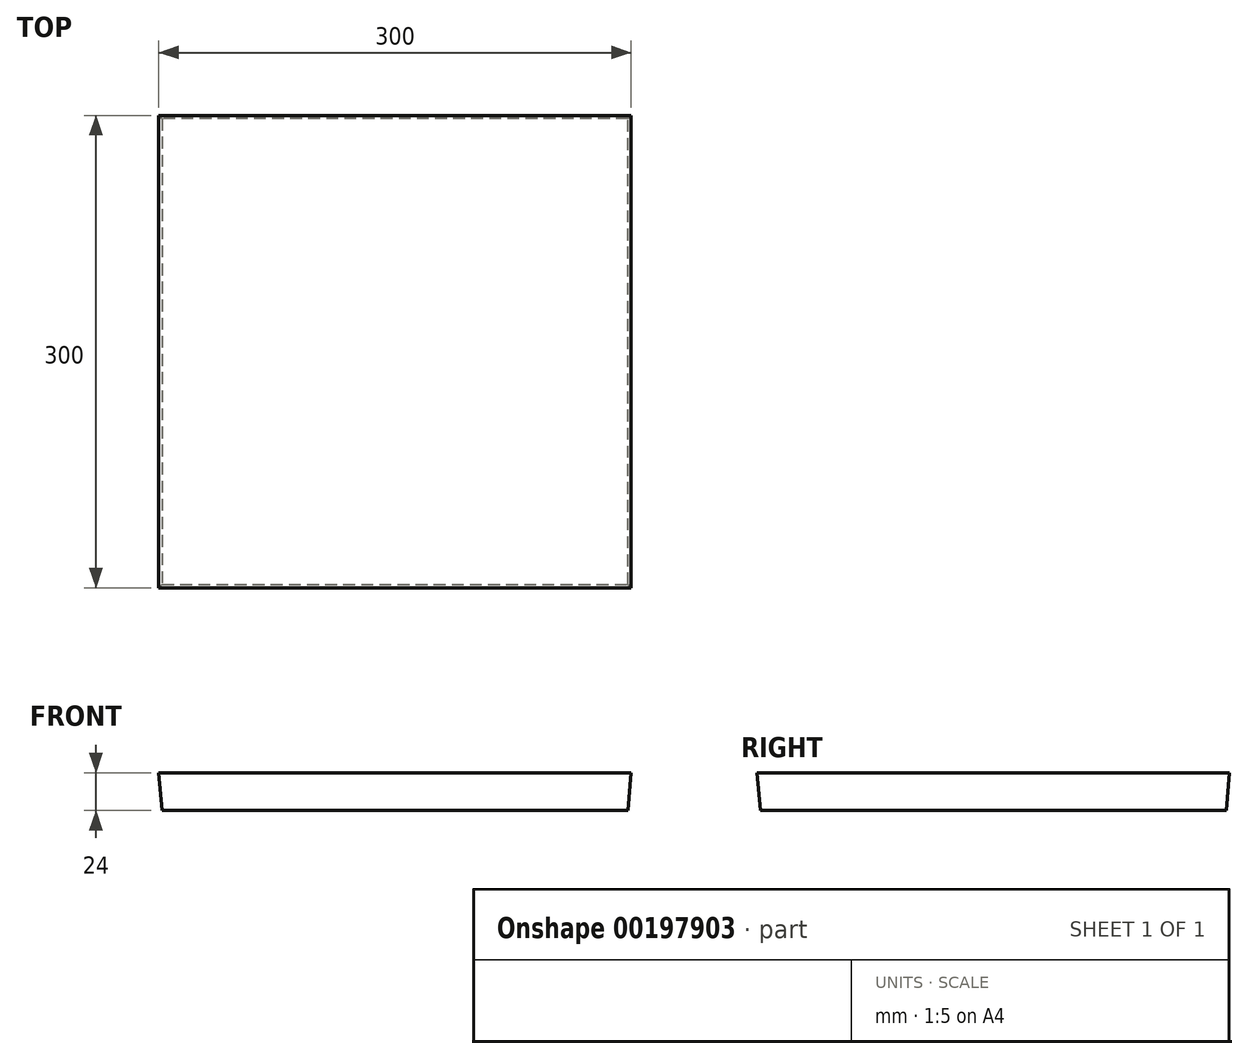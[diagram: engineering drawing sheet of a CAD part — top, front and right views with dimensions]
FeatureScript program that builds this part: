
annotation { "Feature Type Name" : "Feature", "Feature Type Description" : "" }
export const myFeature = defineFeature(function(context is Context, id is Id, definition is map)
    precondition{}
    {
        {
            var Q0;
            Q0=qCreatedBy(makeId("Top.planeOp"),FACE);
            var sketch = newSketch(context, id + "F1", { "sketchPlane" : qUnion([Q0])});
            skLineSegment(sketch, "E0.bottom", {"start": v(-150, 150) * mm, "end": v(150, 150) * mm});
            skLineSegment(sketch, "E0.top", {"start": v(-150, -150) * mm, "end": v(150, -150) * mm});
            skLineSegment(sketch, "E0.left", {"start": v(-150, 150) * mm, "end": v(-150, -150) * mm});
            skLineSegment(sketch, "E0.right", {"start": v(150, 150) * mm, "end": v(150, -150) * mm});
            skSolve(sketch);
        }
        {
            var Q0;
            Q0 = qSketchRegion(id + "F1", true);
            extrude(context, id + "F0", {"entities" : qUnion([Q0]), "oppositeDirection" : true, "depth" : 24 * mm, "hasDraft" : true, "draftAngle" : 5 * degree, "draftPullDirection" : true});
        }
    });
